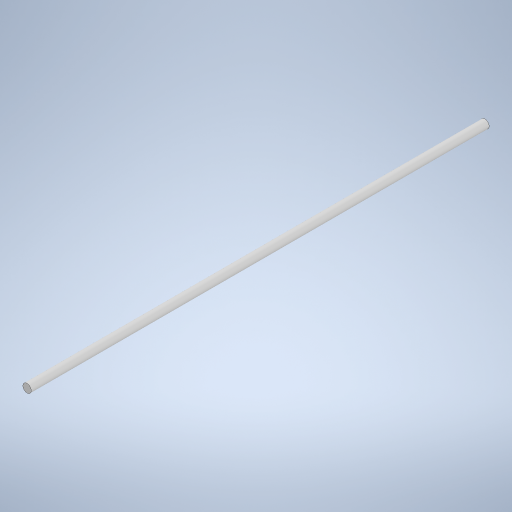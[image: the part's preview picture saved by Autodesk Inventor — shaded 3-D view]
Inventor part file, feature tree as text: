
AUTODESK INVENTOR PART (.ipt)
format: ipt  version: 2024 (Build 280153000, 153)  size: 234,496 bytes
history: native  units: mm
features: extrude x1, sketch x1
ambient origin geometry x8: Origin, YZ Plane, XZ Plane, XY Plane, X Axis, Y Axis, Z Axis, Center Point
bodies: Solid1 (feature_tree)
feature tree (2):
  extrude  "Extrusion1"  Depth=110.0mm TaperAngle=0.0deg
  sketch  "Sketch1"  dims[d0=2.0mm d1=110.0mm d2=0.0mm]
